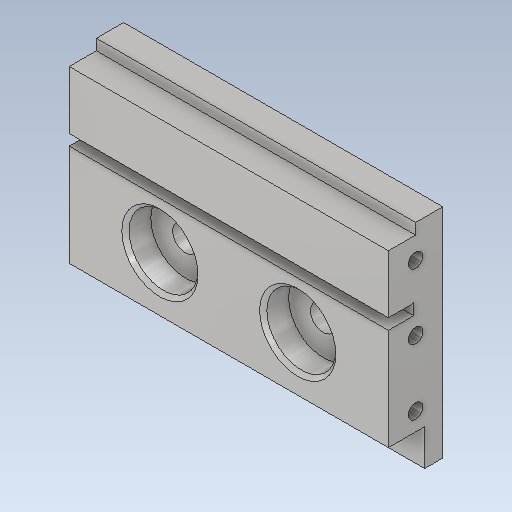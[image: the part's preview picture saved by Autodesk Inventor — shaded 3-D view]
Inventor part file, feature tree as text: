
AUTODESK INVENTOR PART (.ipt)
format: ipt  version: 2020 (Build 240168000, 168)  size: 256,000 bytes
history: native  units: mm
features: sketch x9, extrude x6, hole x3, projected_geometry x3, reference x3, pattern_linear x2, mirror x2, other x2, thread x1, plane x1, chamfer x1
ambient origin geometry x8: Origin, YZ Plane, XZ Plane, XY Plane, X Axis, Y Axis, Z Axis, Center Point
bodies: Solid1 (feature_tree)
feature tree (33):
  extrude  "Extrusion1"  Depth=10.0mm
  extrude  "Extrusion2"  Depth=88.0mm
  hole  "Hole1"  [1 undecoded]
  pattern_linear  "Rectangular Pattern1"  Count1=5 Spacing1=17.0mm
  hole  "Hole2"  [1 undecoded]
  thread  "Thread1"  [1 undecoded]
  pattern_linear  "Rectangular Pattern2"  Count1=3 Spacing1=18.0mm
  plane  "Work Plane1"
  mirror  "Mirror1"
  extrude  "Extrusion3"  Depth=7.0mm TaperAngle=0.0deg
  extrude  "Extrusion4"  Depth=7.0mm
  chamfer  "Chamfer1"  Distance=58.5mm
  mirror  "Mirror2"
  extrude  "Extrusion5"  Depth=29.25mm TaperAngle=0.0deg
  hole  "Hole3"  [1 undecoded]
  extrude  "Extrusion6"  Depth=19.0mm
  sketch  "Sketch1"  dims[d0=88.0mm d1=10.0mm]
  sketch  "Sketch2"  dims[d2=5.0mm d3=0.0mm d4=88.0mm]
  sketch  "Sketch4"  dims[d5=15.0mm d6=50.0mm d7=0.0mm]
  projected_geometry  "Projected Loop1"
  sketch  "Sketch5"  dims[d10=10.0mm]
  sketch  "Sketch6"  dims[d11=5.0mm]
  sketch  "Sketch7"  dims[d12=4.0mm d13=6.0mm d14=8.0mm d15=2.0mm d16=90.0deg d17=10.0mm d18=120.0deg d19=50.0mm d21=17.0mm]
  sketch  "Sketch8"  dims[d22=5.0mm d23=7.5mm]
  projected_geometry  "Projected Loop2"
  sketch  "Sketch9"  dims[d24=4.0mm d25=6.0mm d26=8.0mm d27=2.0mm d28=90.0deg d29=8.0mm d30=120.0deg d31=10.0mm d32=0.0mm d33=30.0mm d35=18.0mm]
  reference  "Reference1"
  reference  "Reference2"
  reference  "Reference3"
  sketch  "Sketch10"  dims[d36=19.0mm d37=7.0mm d38=0.0mm d39=7.0mm d40=58.5mm d41=0.0mm d42=29.25mm d43=0.0mm d44=1.0mm d45=2.0mm d46=45.0deg d47=19.0mm d48=25.0mm d49=3.0mm d50=0.0mm d51=4.0mm d52=6.0mm d53=6.0mm d54=2.0mm d55=90.0deg d56=6.5mm d57=120.0deg d58=7.0mm d59=3.0mm d60=28.0mm d61=114.5mm d62=0.0mm]
  projected_geometry  "Projected Loop3"
  other  "КВ33.000.100 - Блок переключение передач.iam"
  other  "КВ33.000.107 - Крепеж мотора:1"
note: 4 required parameter values undecoded (feature->parameter linkage not recoverable at this tier; creation-order binding heuristic only, values carry confidence <= 0.55)
